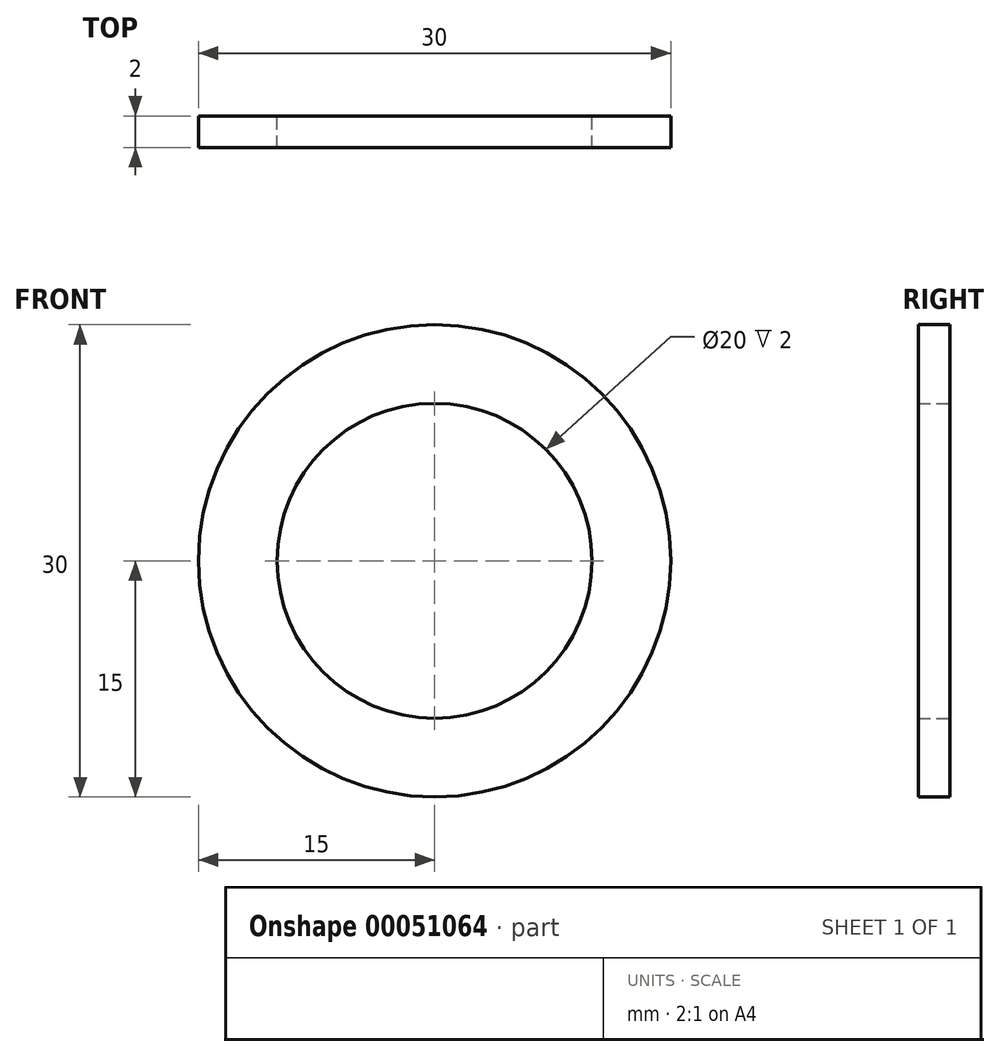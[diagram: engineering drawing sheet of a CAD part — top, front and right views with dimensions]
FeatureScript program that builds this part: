
annotation { "Feature Type Name" : "Feature", "Feature Type Description" : "" }
export const myFeature = defineFeature(function(context is Context, id is Id, definition is map)
    precondition{}
    {
        {
            var Q0;
            Q0=qCreatedBy(makeId("Front.planeOp"),FACE);
            var sketch = newSketch(context, id + "F0", { "sketchPlane" : qUnion([Q0])});
            skCircle(sketch, "E0", {"center": v(0, 0) * mm, "radius": 15 * mm});
            skCircle(sketch, "E1", {"center": v(0, 0) * mm, "radius": 10 * mm});
            skSolve(sketch);
        }
        {
            var Q0;
            Q0=makeQuery(id+"F0.imprint","IMPRINT",FACE,{"disambiguationData":[TD([[makeQuery(id+"F0.imprint","IMPRINT",EDGE,{"derivedFrom":sQuery(id+"F0.wireOp",EDGE,"E0")}),1.0]])]});
            extrude(context, id + "F1", {"entities" : qUnion([Q0]), "depth" : 2 * mm});
        }
    });
